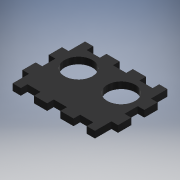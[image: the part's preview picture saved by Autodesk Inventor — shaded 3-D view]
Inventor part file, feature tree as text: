
AUTODESK INVENTOR PART (.ipt)
format: ipt  version: 2019 (Build 230136000, 136)  size: 206,848 bytes
history: native  units: mm
features: extrude x2, sketch x2
ambient origin geometry x8: Origin, YZ Plane, XZ Plane, XY Plane, X Axis, Y Axis, Z Axis, Center Point
bodies: Solid1 (feature_tree)
feature tree (4):
  extrude  "Extrusion1"  Depth=44.0mm
  extrude  "Extrusion2"  Depth=16.0mm
  sketch  "Sketch1"  dims[d0=58.0mm d1=44.0mm]
  sketch  "Sketch2"  dims[d2=17.0mm d3=16.0mm d4=16.0mm d6=4.0mm d7=0.0mm d8=4.0mm d11=8.0mm d12=8.0mm d13=4.0mm d14=4.0mm d15=0.0mm d16=4.0mm d17=8.0mm d18=26.0mm]
